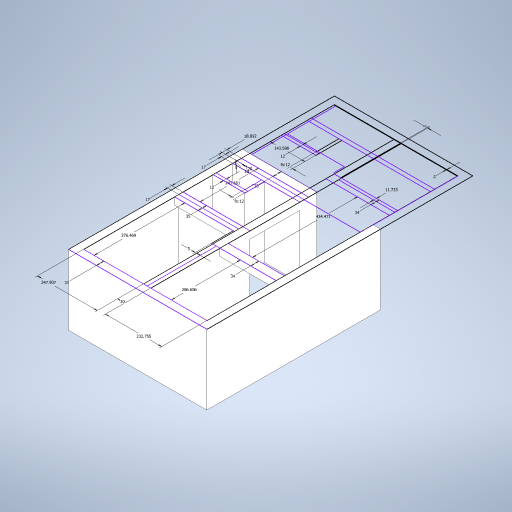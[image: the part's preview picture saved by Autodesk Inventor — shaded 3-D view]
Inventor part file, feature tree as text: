
AUTODESK INVENTOR PART (.ipt)
format: ipt  version: 2024 (Build 280153000, 153)  size: 375,296 bytes
history: native  units: in
note: dims shown in document units (in); Inventor stores cm internally (conversion verified against a paired STEP export)
features: sketch x5, extrude x2
ambient origin geometry x8: Origin, YZ Plane, XZ Plane, XY Plane, X Axis, Y Axis, Z Axis, Center Point
bodies: Solid1 (feature_tree)
feature tree (7):
  sketch  "Sketch1"  dims[d1=12.2047in d2=148.2162in]
  extrude  "Extrusion1"  Depth=148.2162in
  extrude  "Extrusion2"  Depth=13.7795in
  sketch  "Sketch2"  dims[d3=13.7795in d4=13.7795in]
  sketch  "Sketch3"  dims[d5=95.142in]
  sketch  "Sketch4"  dims[d7=4.7244in]
  sketch  "Sketch5"  dims[d8=56.5305in d9=4.7244in d10=13.3858in d11=13.3858in d12=112.8368in d13=171.0516in d14=11.811in d15=97.6011in d16=91.6359in d17=4.6192in d18=0.7874in d19=1.1811in d20=6.6929in d21=7.4378in d22=4.7244in d23=4.7244in d24=6.6929in d25=1.9685in d26=11.811in d27=0.0in d28=114.1732in d29=0.0in d30=0.7874in d31=1.5748in d33=0.9843in d34=0.3937in d36=0.3937in d38=2.3622in d40=0.9843in d41=0.3937in d43=0.3937in d45=0.7874in d46=1.9685in d47=3.937in d48=7.874in d49=2.3622in]
